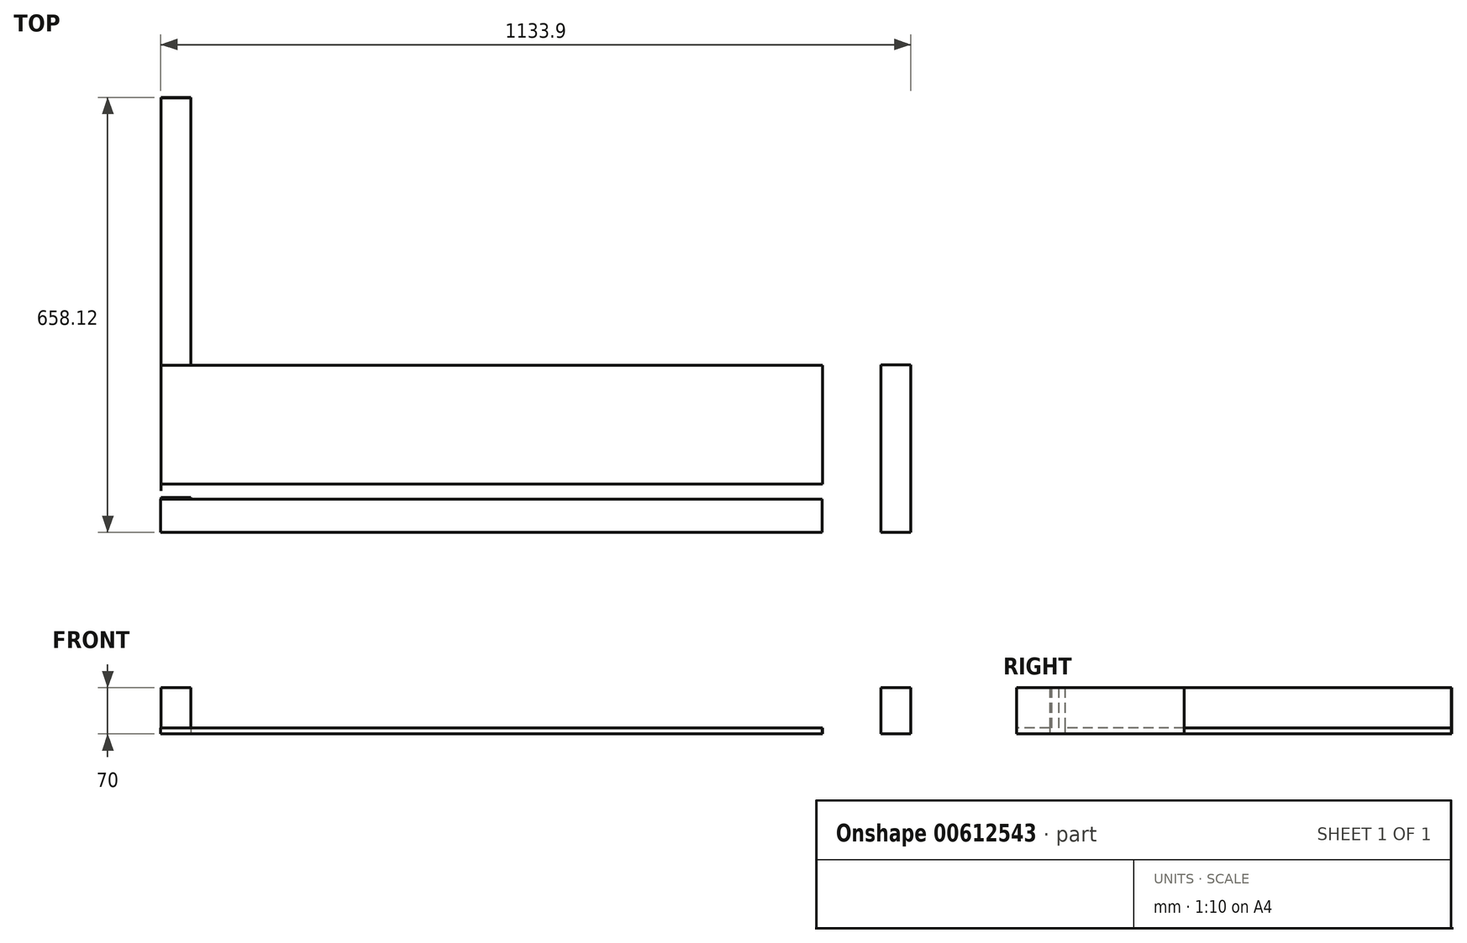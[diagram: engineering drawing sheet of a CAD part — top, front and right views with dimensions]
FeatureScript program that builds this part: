
annotation { "Feature Type Name" : "Feature", "Feature Type Description" : "" }
export const myFeature = defineFeature(function(context is Context, id is Id, definition is map)
    precondition{}
    {
        {
            var Q0;
            Q0=qCreatedBy(makeId("Top.planeOp"),FACE);
            var sketch = newSketch(context, id + "F0", { "sketchPlane" : qUnion([Q0])});
            skLineSegment(sketch, "E0.bottom", {"start": v(-500, 623.37) * mm, "end": v(500, 623.37) * mm});
            skLineSegment(sketch, "E0.top", {"start": v(-500, -576.63) * mm, "end": v(500, -576.63) * mm});
            skLineSegment(sketch, "E0.left", {"start": v(-500, 623.37) * mm, "end": v(-500, -576.63) * mm});
            skLineSegment(sketch, "E0.right", {"start": v(500, 623.37) * mm, "end": v(500, -576.63) * mm});
            skPoint(sketch, "E0.middle", {"position": v(0, 23.37) * mm});
            skLineSegment(sketch, "E1.bottom", {"start": v(-500.06, 18.73) * mm, "end": v(-455.06, 18.73) * mm});
            skLineSegment(sketch, "E1.top", {"start": v(-500.06, -576.27) * mm, "end": v(-455.06, -576.27) * mm});
            skLineSegment(sketch, "E1.left", {"start": v(-500.06, 18.73) * mm, "end": v(-500.06, -576.27) * mm});
            skLineSegment(sketch, "E1.right", {"start": v(-455.06, 18.73) * mm, "end": v(-455.06, -576.27) * mm});
            skPoint(sketch, "E1.middle", {"position": v(-477.56, -278.77) * mm});
            skPoint(sketch, "E2.middle", {"position": v(436.34, -28.05) * mm});
            skLineSegment(sketch, "E3.bottom", {"start": v(-500.2, 624.3) * mm, "end": v(-455.2, 624.3) * mm});
            skLineSegment(sketch, "E3.top", {"start": v(-500.2, 29.3) * mm, "end": v(-455.2, 29.3) * mm});
            skLineSegment(sketch, "E3.left", {"start": v(-500.2, 624.3) * mm, "end": v(-500.2, 29.3) * mm});
            skLineSegment(sketch, "E3.right", {"start": v(-455.2, 624.3) * mm, "end": v(-455.2, 29.3) * mm});
            skPoint(sketch, "E3.middle", {"position": v(-477.7, 326.8) * mm});
            skLineSegment(sketch, "E4.bottom", {"start": v(-500, 219.13) * mm, "end": v(500, 219.13) * mm});
            skLineSegment(sketch, "E4.top", {"start": v(-500, 39.13) * mm, "end": v(500, 39.13) * mm});
            skLineSegment(sketch, "E4.left", {"start": v(-500, 219.13) * mm, "end": v(-500, 39.13) * mm});
            skLineSegment(sketch, "E4.right", {"start": v(500, 219.13) * mm, "end": v(500, 39.13) * mm});
            skPoint(sketch, "E4.middle", {"position": v(0, 129.13) * mm});
            skLineSegment(sketch, "E5.bottom", {"start": v(-500.38, 16.17) * mm, "end": v(499.62, 16.17) * mm});
            skLineSegment(sketch, "E5.top", {"start": v(-500.38, -33.83) * mm, "end": v(499.62, -33.83) * mm});
            skLineSegment(sketch, "E5.left", {"start": v(-500.38, 16.17) * mm, "end": v(-500.38, -33.83) * mm});
            skLineSegment(sketch, "E5.right", {"start": v(499.62, 16.17) * mm, "end": v(499.62, -33.83) * mm});
            skPoint(sketch, "E5.middle", {"position": v(-0.38, -8.83) * mm});
            skLineSegment(sketch, "E6.bottom", {"start": v(588.52, 219.32) * mm, "end": v(633.52, 219.32) * mm});
            skLineSegment(sketch, "E6.top", {"start": v(588.52, -33.68) * mm, "end": v(633.52, -33.68) * mm});
            skLineSegment(sketch, "E6.left", {"start": v(588.52, 219.32) * mm, "end": v(588.52, -33.68) * mm});
            skLineSegment(sketch, "E6.right", {"start": v(633.52, 219.32) * mm, "end": v(633.52, -33.68) * mm});
            skPoint(sketch, "E6.middle", {"position": v(611.02, 92.82) * mm});
            skSolve(sketch);
        }
        {
            var Q0;
            Q0=makeQuery(id+"F0.imprint","IMPRINT",FACE,{"disambiguationData":[TD([[makeQuery(id+"F0.imprint","IMPRINT",EDGE,{"derivedFrom":sQuery(id+"F0.wireOp",EDGE,"E0.bottom")}),-1.0]])]});
            extrude(context, id + "F1", {"entities" : qUnion([Q0]), "depth" : 9 * mm, "offsetDistance" : 25 * mm});
        }
        {
            var Q0;
            Q0=makeQuery(id+"F0.imprint","IMPRINT",FACE,{"disambiguationData":[TD([[makeQuery(id+"F0.imprint","IMPRINT",EDGE,{"derivedFrom":sQuery(id+"F0.wireOp",EDGE,"E4.bottom")}),-1.0]])]});
            extrude(context, id + "F2", {"entities" : qUnion([Q0]), "depth" : 9 * mm, "offsetDistance" : 25 * mm});
        }
        {
            var Q0;
            Q0=makeQuery(id+"F0.imprint","IMPRINT",FACE,{"disambiguationData":[TD([[makeQuery(id+"F0.imprint","IMPRINT",EDGE,{"derivedFrom":sQuery(id+"F0.wireOp",EDGE,"E5.bottom")}),-1.0]])]});
            extrude(context, id + "F3", {"entities" : qUnion([Q0]), "depth" : 9 * mm, "offsetDistance" : 25 * mm});
        }
        {
            var Q0;
            Q0=makeQuery(id+"F0.imprint","IMPRINT",FACE,{"disambiguationData":[TD([[makeQuery(id+"F0.imprint","IMPRINT",EDGE,{"derivedFrom":sQuery(id+"F0.wireOp",EDGE,"E1.bottom")}),-1.0]])]});
            extrude(context, id + "F4", {"entities" : qUnion([Q0]), "depth" : 70 * mm, "offsetDistance" : 25 * mm});
        }
        {
            var Q0;
            Q0=makeQuery(id+"F0.imprint","IMPRINT",FACE,{"disambiguationData":[TD([[makeQuery(id+"F0.imprint","IMPRINT",EDGE,{"derivedFrom":sQuery(id+"F0.wireOp",EDGE,"E3.bottom")}),-1.0]])]});
            extrude(context, id + "F5", {"entities" : qUnion([Q0]), "depth" : 70 * mm, "offsetDistance" : 25 * mm});
        }
        {
            var Q0;
            Q0=makeQuery(id+"F0.imprint","IMPRINT",FACE,{"disambiguationData":[TD([[makeQuery(id+"F0.imprint","IMPRINT",EDGE,{"derivedFrom":sQuery(id+"F0.wireOp",EDGE,"E6.bottom")}),-1.0]])]});
            extrude(context, id + "F6", {"entities" : qUnion([Q0]), "depth" : 70 * mm, "offsetDistance" : 25 * mm});
        }
    });
